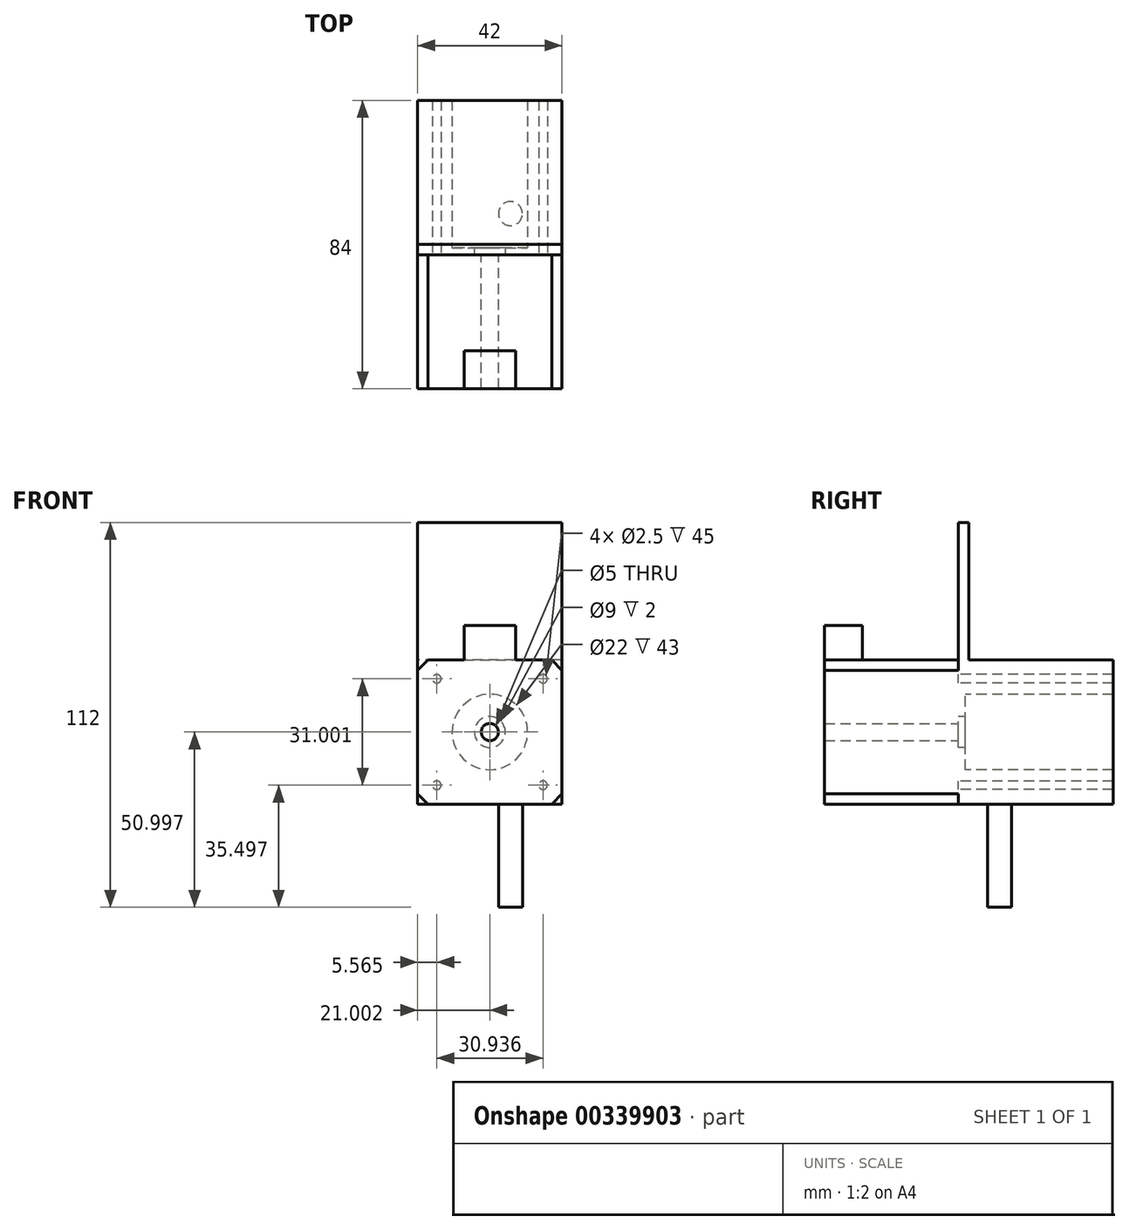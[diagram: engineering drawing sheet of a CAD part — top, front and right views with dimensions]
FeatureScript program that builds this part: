
annotation { "Feature Type Name" : "Feature", "Feature Type Description" : "" }
export const myFeature = defineFeature(function(context is Context, id is Id, definition is map)
    precondition{}
    {
        {
            var Q0;
            Q0=qCreatedBy(makeId("Front.planeOp"),FACE);
            var sketch = newSketch(context, id + "F0", { "sketchPlane" : qUnion([Q0])});
            skPoint(sketch, "E0.endSnap0", {"position": v(-3.05, 11.23) * mm});
            skLineSegment(sketch, "E1", {"start": v(-52.99, 22.73) * mm, "end": v(7.01, 22.62) * mm, "construction": true});
            skLineSegment(sketch, "E2", {"start": v(-22.99, 42.42) * mm, "end": v(-22.99, -22.58) * mm, "construction": true});
            skPoint(sketch, "E2.endSnap0", {"position": v(-22.99, -22.58) * mm});
            skCircle(sketch, "E3", {"center": v(-22.99, 22.68) * mm, "radius": 11 * mm});
            skLineSegment(sketch, "E4", {"start": v(-38.42, 43.83) * mm, "end": v(-38.42, -3.17) * mm, "construction": true});
            skLineSegment(sketch, "E5", {"start": v(-7.49, 43.73) * mm, "end": v(-7.49, -3.27) * mm, "construction": true});
            skLineSegment(sketch, "E6", {"start": v(-47.74, 7.18) * mm, "end": v(-4.74, 7.18) * mm, "construction": true});
            skCircle(sketch, "E7", {"center": v(-38.42, 38.18) * mm, "radius": 1.25 * mm});
            skCircle(sketch, "E8", {"center": v(-7.49, 38.18) * mm, "radius": 1.25 * mm});
            skCircle(sketch, "E9", {"center": v(-38.42, 7.18) * mm, "radius": 1.25 * mm});
            skCircle(sketch, "E10", {"center": v(-7.49, 7.18) * mm, "radius": 1.25 * mm});
            skCircle(sketch, "E11", {"center": v(-22.99, 22.68) * mm, "radius": 2.5 * mm});
            skCircle(sketch, "E12", {"center": v(-22.99, 22.68) * mm, "radius": 4.5 * mm});
            skLineSegment(sketch, "E13.bottom", {"start": v(-43.99, 43.68) * mm, "end": v(-1.99, 43.68) * mm});
            skLineSegment(sketch, "E13.top", {"start": v(-43.99, 1.68) * mm, "end": v(-1.99, 1.68) * mm});
            skLineSegment(sketch, "E13.left", {"start": v(-43.99, 43.68) * mm, "end": v(-43.99, 1.68) * mm});
            skLineSegment(sketch, "E13.right", {"start": v(-1.99, 43.68) * mm, "end": v(-1.99, 1.68) * mm});
            skSolve(sketch);
        }
        {
            var Q0;
            Q0=makeQuery(id+"F0.imprint","IMPRINT",FACE,{"disambiguationData":[TD([[makeQuery(id+"F0.imprint","IMPRINT",EDGE,{"derivedFrom":sQuery(id+"F0.wireOp",EDGE,"E3")}),1.0]])]});
            var Q1;
            Q1=makeQuery(id+"F0.imprint","IMPRINT",FACE,{"disambiguationData":[TD([[makeQuery(id+"F0.imprint","IMPRINT",EDGE,{"derivedFrom":sQuery(id+"F0.wireOp",EDGE,"E11")}),-1.0]])]});
            var Q2;
            Q2=makeQuery(id+"F0.imprint","IMPRINT",FACE,{"disambiguationData":[TD([[makeQuery(id+"F0.imprint","IMPRINT",EDGE,{"derivedFrom":sQuery(id+"F0.wireOp",EDGE,"E3")}),-1.0]])]});
            var Q3;
            Q3=makeQuery(id+"F0.imprint","IMPRINT",FACE,{"disambiguationData":[TD([[makeQuery(id+"F0.imprint","IMPRINT",EDGE,{"derivedFrom":sQuery(id+"F0.wireOp",EDGE,"E7")}),1.0]])]});
            var Q4;
            Q4=makeQuery(id+"F0.imprint","IMPRINT",FACE,{"disambiguationData":[TD([[makeQuery(id+"F0.imprint","IMPRINT",EDGE,{"derivedFrom":sQuery(id+"F0.wireOp",EDGE,"E10")}),1.0]])]});
            var Q5;
            Q5=makeQuery(id+"F0.imprint","IMPRINT",FACE,{"disambiguationData":[TD([[makeQuery(id+"F0.imprint","IMPRINT",EDGE,{"derivedFrom":sQuery(id+"F0.wireOp",EDGE,"E9")}),1.0]])]});
            var Q6;
            Q6=makeQuery(id+"F0.imprint","IMPRINT",FACE,{"disambiguationData":[TD([[makeQuery(id+"F0.imprint","IMPRINT",EDGE,{"derivedFrom":sQuery(id+"F0.wireOp",EDGE,"E8")}),1.0]])]});
            extrude(context, id + "F1", {"entities" : qUnion([Q0, Q1, Q2, Q3, Q4, Q5, Q6]), "offsetDistance" : 25 * mm, "depth" : 39 * mm});
        }
        {
            var Q0;
            Q0=makeQuery(id+"F1.opExtrude","SWEPT_EDGE",EDGE,{"disambiguationData":[OSD([sQuery(id+"F0.wireOp",EDGE,"E13.top"),sQuery(id+"F0.wireOp",EDGE,"E13.left")])]});
            var Q1;
            Q1=makeQuery(id+"F1.opExtrude","SWEPT_EDGE",EDGE,{"disambiguationData":[OSD([sQuery(id+"F0.wireOp",EDGE,"E13.top"),sQuery(id+"F0.wireOp",EDGE,"E13.right")])]});
            var Q2;
            Q2=makeQuery(id+"F1.opExtrude","SWEPT_EDGE",EDGE,{"disambiguationData":[OSD([sQuery(id+"F0.wireOp",EDGE,"E13.bottom"),sQuery(id+"F0.wireOp",EDGE,"E13.right")])]});
            var Q3;
            Q3=makeQuery(id+"F1.opExtrude","SWEPT_EDGE",EDGE,{"disambiguationData":[OSD([sQuery(id+"F0.wireOp",EDGE,"E13.bottom"),sQuery(id+"F0.wireOp",EDGE,"E13.left")])]});
            chamfer(context, id + "F2", {"entities" : qUnion([Q0, Q1, Q2, Q3]), "width" : 3 * mm, "tangentPropagation" : true});
        }
        {
            var Q0;
            Q0=makeQuery(id+"F0.imprint","IMPRINT",FACE,{"disambiguationData":[TD([[makeQuery(id+"F0.imprint","IMPRINT",EDGE,{"derivedFrom":sQuery(id+"F0.wireOp",EDGE,"E3")}),1.0]])]});
            extrude(context, id + "F3", {"entities" : qUnion([Q0]), "operationType" : NewBodyOperationType.ADD, "depth" : -2 * mm});
        }
        {
            var Q0;
            Q0=sQuery(id+"F0.wireOp",EDGE,"E8");
            var Q1;
            Q1=sQuery(id+"F0.wireOp",EDGE,"E10");
            var Q2;
            Q2=sQuery(id+"F0.wireOp",EDGE,"E7");
            var Q3;
            Q3=sQuery(id+"F0.wireOp",EDGE,"E9");
            extrude(context, id + "F4", {"bodyType" : ExtendedToolBodyType.SURFACE, "operationType" : NewBodyOperationType.REMOVE, "surfaceEntities" : qUnion([Q0, Q1, Q2, Q3]), "depth" : 4 * mm});
        }
        {
            var Q0;
            Q0=makeQuery(id+"F1.opExtrude","SWEPT_FACE",FACE,{"disambiguationData":[OSD([sQuery(id+"F0.wireOp",EDGE,"E13.bottom")])]});
            var sketch = newSketch(context, id + "F5", { "sketchPlane" : qUnion([Q0])});
            skLineSegment(sketch, "E14.bottom", {"start": v(-30.49, -39) * mm, "end": v(-15.49, -39) * mm});
            skLineSegment(sketch, "E14.top", {"start": v(-30.49, -28) * mm, "end": v(-15.49, -28) * mm});
            skLineSegment(sketch, "E14.left", {"start": v(-30.49, -39) * mm, "end": v(-30.49, -28) * mm});
            skLineSegment(sketch, "E14.right", {"start": v(-15.49, -39) * mm, "end": v(-15.49, -28) * mm});
            skSolve(sketch);
        }
        {
            var Q0;
            Q0=makeQuery(id+"F5.imprint","IMPRINT",FACE,{"disambiguationData":[TD([[makeQuery(id+"F5.imprint","IMPRINT",EDGE,{"derivedFrom":sQuery(id+"F5.wireOp",EDGE,"E14.bottom")}),1.0]])]});
            extrude(context, id + "F6", {"entities" : qUnion([Q0]), "operationType" : NewBodyOperationType.ADD, "depth" : 10 * mm, "offsetDistance" : 25 * mm});
        }
        {
            var Q0;
            Q0 = qSketchRegion(id + "F0", true);
            extrude(context, id + "F7", {"entities" : qUnion([Q0]), "operationType" : NewBodyOperationType.ADD, "oppositeDirection" : true, "depth" : 45 * mm, "offsetDistance" : 25 * mm});
        }
        {
            var Q0;
            {var subQ0=sQuery(id+"F0.wireOp",EDGE,"E13.bottom");Q0=makeQuery(id+"F7.boolean.opBoolean","MERGE",FACE,{"derivedFrom":[makeQuery(id+"F1.opExtrude","SWEPT_FACE",FACE,{"disambiguationData":[OSD([subQ0])]}),makeQuery(id+"F7.opExtrude","SWEPT_FACE",FACE,{"disambiguationData":[OSD([subQ0])]})]});}
            var sketch = newSketch(context, id + "F8", { "sketchPlane" : qUnion([Q0])});
            skLineSegment(sketch, "E15", {"start": v(-1.99, 3) * mm, "end": v(-43.99, 3) * mm});
            skLineSegment(sketch, "E16", {"start": v(-43.99, 3) * mm, "end": v(-43.99, 0) * mm});
            skLineSegment(sketch, "E17", {"start": v(-43.99, 0) * mm, "end": v(-1.99, 0) * mm});
            skLineSegment(sketch, "E18", {"start": v(-1.99, 0) * mm, "end": v(-1.99, 3) * mm});
            skSolve(sketch);
        }
        {
            var Q0;
            Q0 = qSketchRegion(id + "F8", true);
            extrude(context, id + "F9", {"entities" : qUnion([Q0]), "operationType" : NewBodyOperationType.ADD, "depth" : 40 * mm, "offsetDistance" : 25 * mm});
        }
        {
            var Q0;
            {var subQ0=sQuery(id+"F0.wireOp",EDGE,"E13.top");Q0=makeQuery(id+"F7.boolean.opBoolean","MERGE",FACE,{"derivedFrom":[makeQuery(id+"F1.opExtrude","SWEPT_FACE",FACE,{"disambiguationData":[OSD([subQ0])]}),makeQuery(id+"F7.opExtrude","SWEPT_FACE",FACE,{"disambiguationData":[OSD([subQ0])]})]});}
            var sketch = newSketch(context, id + "F10", { "sketchPlane" : qUnion([Q0])});
            skLineSegment(sketch, "E19", {"start": v(-1.99, -12) * mm, "end": v(-43.99, -12) * mm});
            skCircle(sketch, "E20", {"center": v(-16.99, -12) * mm, "radius": 3.5 * mm});
            skSolve(sketch);
        }
        {
            var Q0;
            {var subQ0=sQuery(id+"F10.wireOp",EDGE,"E20");var subQ1=sQuery(id+"F10.wireOp",EDGE,"E19");var subQ2=makeQuery(id+"F10.imprint","INTERSECT",VERTEX,{"disambiguationData":[OD(0.0)],"derivedFrom":[subQ1,subQ0]});Q0=makeQuery(id+"F10.imprint","IMPRINT",FACE,{"disambiguationData":[TD([[makeQuery(id+"F10.imprint","IMPRINT",EDGE,{"disambiguationData":[TD([[subQ2,-1.0]])],"derivedFrom":subQ1}),-1.0]])]});}
            var Q1;
            {var subQ0=sQuery(id+"F10.wireOp",EDGE,"E20");var subQ1=sQuery(id+"F10.wireOp",EDGE,"E19");var subQ2=makeQuery(id+"F10.imprint","INTERSECT",VERTEX,{"disambiguationData":[OD(0.0)],"derivedFrom":[subQ1,subQ0]});Q1=makeQuery(id+"F10.imprint","IMPRINT",FACE,{"disambiguationData":[TD([[makeQuery(id+"F10.imprint","IMPRINT",EDGE,{"disambiguationData":[TD([[subQ2,-1.0]])],"derivedFrom":subQ1}),1.0]])]});}
            var Q2;
            Q2=sQuery(id+"F10.wireOp",EDGE,"E20");
            extrude(context, id + "F11", {"entities" : qUnion([Q0, Q1]), "surfaceOperationType" : NewSurfaceOperationType.ADD, "surfaceEntities" : qUnion([Q2]), "depth" : 30 * mm, "offsetDistance" : 25 * mm});
        }
        {
            var Q0;
            Q0=sQuery(id+"F10.wireOp",EDGE,"E20");
            extrude(context, id + "F12", {"bodyType" : ExtendedToolBodyType.SURFACE, "operationType" : NewBodyOperationType.REMOVE, "surfaceEntities" : qUnion([Q0]), "oppositeDirection" : true, "depth" : 44 * mm, "offsetDistance" : 25 * mm});
        }
    });
